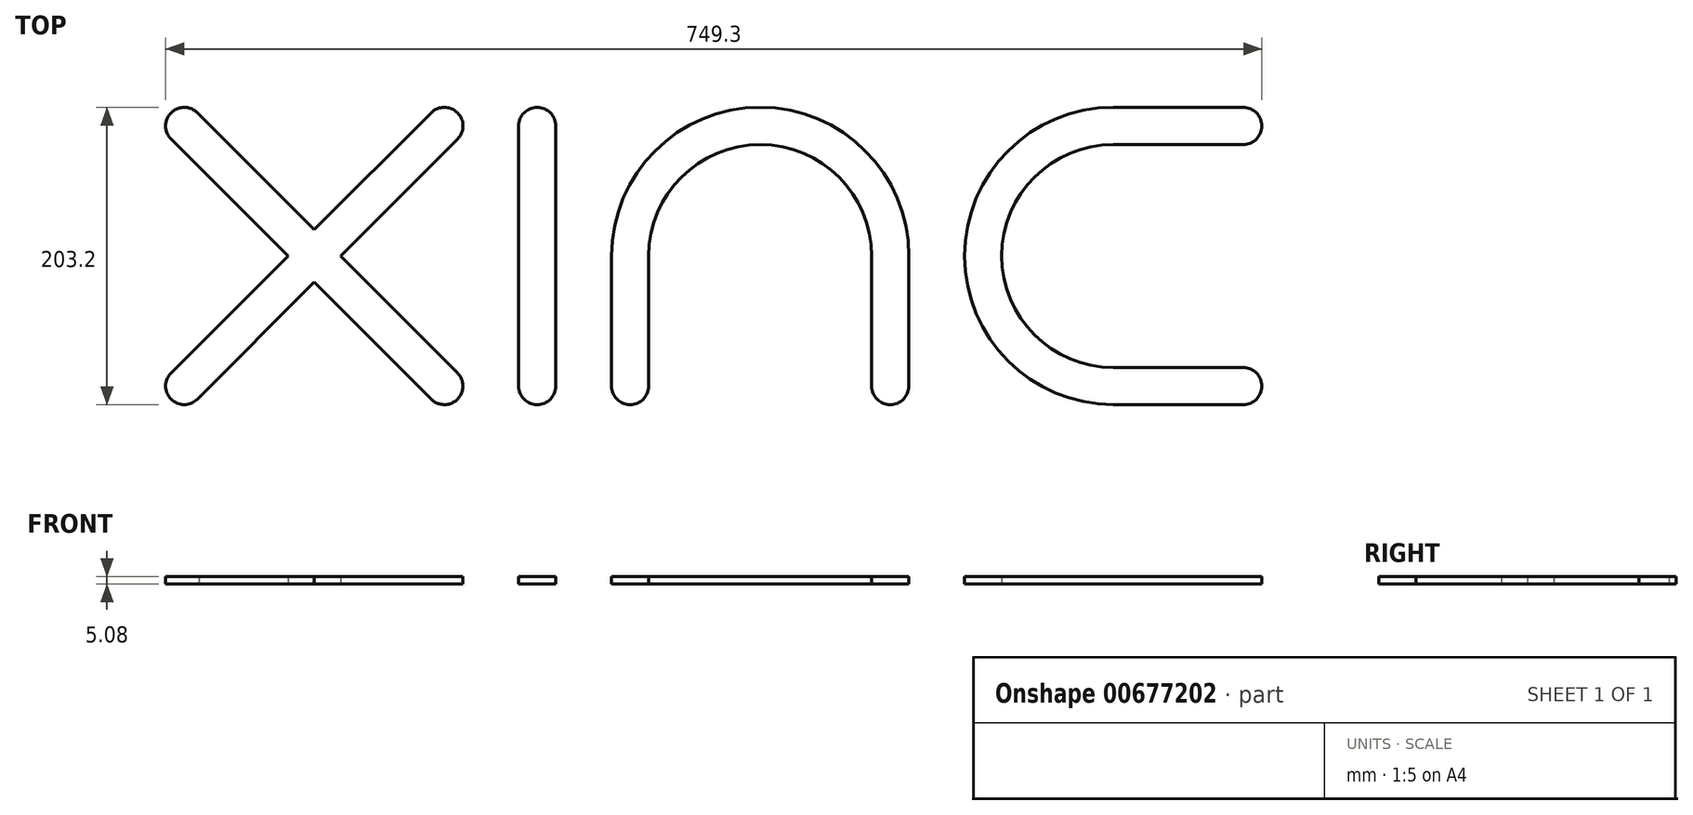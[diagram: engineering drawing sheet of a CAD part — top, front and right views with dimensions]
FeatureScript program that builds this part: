
annotation { "Feature Type Name" : "Feature", "Feature Type Description" : "" }
export const myFeature = defineFeature(function(context is Context, id is Id, definition is map)
    precondition{}
    {
        {
            var Q0;
            Q0=qCreatedBy(makeId("Top.planeOp"),FACE);
            var sketch = newSketch(context, id + "F0", { "sketchPlane" : qUnion([Q0])});
            skArc(sketch, "E0", {"start": v(-282.12, 96.75) * mm, "mid": v(-300.53, 98.4) * mm, "end": v(-301.08, 79.92) * mm});
            skArc(sketch, "E1", {"start": v(-123.28, -97.88) * mm, "mid": v(-105.32, -97.88) * mm, "end": v(-105.32, -79.92) * mm});
            skArc(sketch, "E2", {"start": v(-105.32, 79.92) * mm, "mid": v(-105.32, 97.88) * mm, "end": v(-123.28, 97.88) * mm});
            skArc(sketch, "E3", {"start": v(-301.08, -79.92) * mm, "mid": v(-301.08, -97.88) * mm, "end": v(-283.12, -97.88) * mm});
            skLineSegment(sketch, "E4", {"start": v(-301.08, 79.92) * mm, "end": v(-221.16, 0) * mm});
            skLineSegment(sketch, "E5", {"start": v(-282.12, 96.75) * mm, "end": v(-203.24, 17.93) * mm});
            skLineSegment(sketch, "E6", {"start": v(-123.28, 97.88) * mm, "end": v(-203.24, 17.93) * mm});
            skLineSegment(sketch, "E7", {"start": v(-283.12, -97.88) * mm, "end": v(-203.2, -17.96) * mm});
            skLineSegment(sketch, "E8", {"start": v(-292.1, -88.9) * mm, "end": v(-114.3, 88.9) * mm, "construction": true});
            skLineSegment(sketch, "E9", {"start": v(-292.1, 88.9) * mm, "end": v(-114.3, -88.9) * mm, "construction": true});
            skPoint(sketch, "E10", {"position": v(-203.2, 0) * mm});
            skLineSegment(sketch, "E11.trimOffspring", {"start": v(-221.16, 0) * mm, "end": v(-301.08, -79.92) * mm});
            skLineSegment(sketch, "E12.trimOffspring", {"start": v(-203.2, -17.96) * mm, "end": v(-123.28, -97.88) * mm});
            skLineSegment(sketch, "E13.trimOffspring", {"start": v(-185.27, -0.03) * mm, "end": v(-105.32, -79.92) * mm});
            skLineSegment(sketch, "E14.trimOffspring", {"start": v(-185.27, -0.03) * mm, "end": v(-105.32, 79.92) * mm});
            skArc(sketch, "E15", {"start": v(-38.1, 88.9) * mm, "mid": v(-50.8, 101.6) * mm, "end": v(-63.5, 88.9) * mm});
            skArc(sketch, "E16", {"start": v(-63.5, -88.9) * mm, "mid": v(-50.8, -101.6) * mm, "end": v(-38.1, -88.9) * mm});
            skLineSegment(sketch, "E17", {"start": v(-63.5, 88.9) * mm, "end": v(-63.5, -88.9) * mm});
            skLineSegment(sketch, "E18", {"start": v(-38.1, 88.9) * mm, "end": v(-38.1, -88.9) * mm});
            skLineSegment(sketch, "E19", {"start": v(-292.1, 88.9) * mm, "end": v(469.7, 88.9) * mm, "construction": true});
            skLineSegment(sketch, "E20", {"start": v(-292.1, -88.9) * mm, "end": v(469.7, -88.9) * mm, "construction": true});
            skArc(sketch, "E21", {"start": v(0, -88.9) * mm, "mid": v(12.7, -101.6) * mm, "end": v(25.4, -88.9) * mm});
            skArc(sketch, "E22", {"start": v(177.8, -88.9) * mm, "mid": v(190.5, -101.6) * mm, "end": v(203.2, -88.9) * mm});
            skPoint(sketch, "E23.center.orphan", {"position": v(12.7, 88.9) * mm});
            skLineSegment(sketch, "E24", {"start": v(0, -88.9) * mm, "end": v(0, 0) * mm});
            skArc(sketch, "E25", {"start": v(177.8, 0) * mm, "mid": v(101.6, 76.2) * mm, "end": v(25.4, 0) * mm});
            skLineSegment(sketch, "E26", {"start": v(25.4, -88.9) * mm, "end": v(25.4, 0) * mm});
            skLineSegment(sketch, "E27", {"start": v(203.2, 0) * mm, "end": v(203.2, -88.9) * mm});
            skLineSegment(sketch, "E28", {"start": v(177.8, -88.9) * mm, "end": v(177.8, 0) * mm});
            skArc(sketch, "E29.trimOffspring", {"start": v(203.2, 0) * mm, "mid": v(101.6, 101.6) * mm, "end": v(0, 0) * mm});
            skArc(sketch, "E30", {"start": v(342.9, 76.2) * mm, "mid": v(266.7, 0) * mm, "end": v(342.9, -76.2) * mm});
            skArc(sketch, "E31", {"start": v(431.8, 76.2) * mm, "mid": v(444.5, 88.9) * mm, "end": v(431.8, 101.6) * mm});
            skArc(sketch, "E32", {"start": v(431.8, -101.6) * mm, "mid": v(444.5, -88.9) * mm, "end": v(431.8, -76.2) * mm});
            skLineSegment(sketch, "E33", {"start": v(431.8, 76.2) * mm, "end": v(342.9, 76.2) * mm});
            skLineSegment(sketch, "E34", {"start": v(431.8, 101.6) * mm, "end": v(342.9, 101.6) * mm});
            skLineSegment(sketch, "E35", {"start": v(431.8, -101.6) * mm, "end": v(342.9, -101.6) * mm});
            skLineSegment(sketch, "E36", {"start": v(431.8, -76.2) * mm, "end": v(342.9, -76.2) * mm});
            skArc(sketch, "E37.trimOffspring", {"start": v(342.9, 101.6) * mm, "mid": v(241.3, 0) * mm, "end": v(342.9, -101.6) * mm});
            skCircle(sketch, "E38", {"center": v(254, 0) * mm, "radius": 12.7 * mm, "construction": true});
            skSolve(sketch);
        }
        {
            var Q0;
            Q0=qSketchRegion(id+"F0",true);
            extrude(context, id + "F1", {"entities" : qUnion([Q0]), "depth" : 5.08 * mm, "offsetDistance" : 25.4 * mm});
        }
    });
